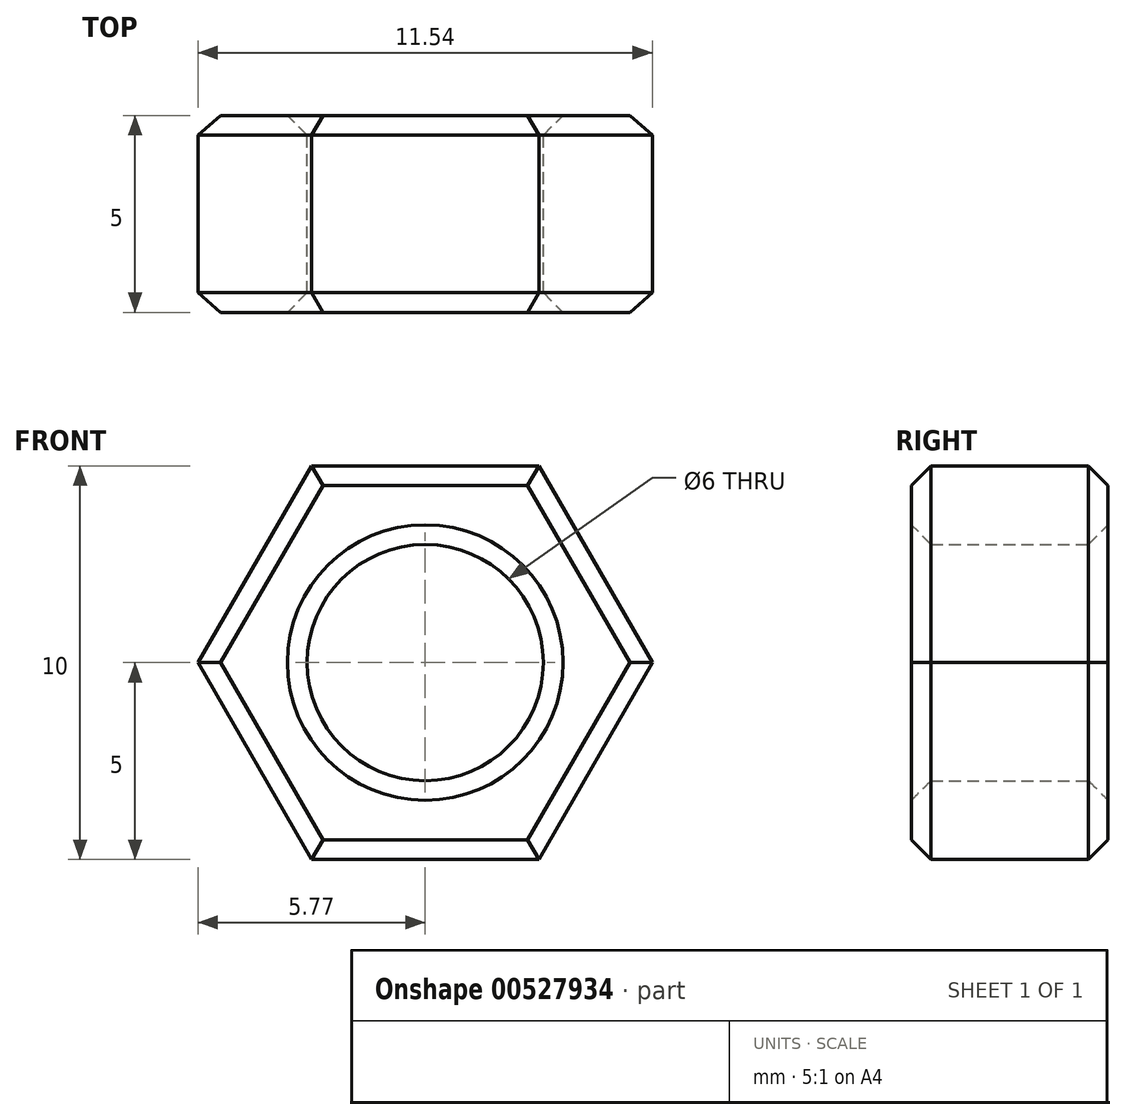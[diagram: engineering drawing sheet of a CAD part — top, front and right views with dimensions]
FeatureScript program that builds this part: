
annotation { "Feature Type Name" : "Feature", "Feature Type Description" : "" }
export const myFeature = defineFeature(function(context is Context, id is Id, definition is map)
    precondition{}
    {
        {
            var Q0;
            Q0=qCreatedBy(makeId("Front.planeOp"),FACE);
            var sketch = newSketch(context, id + "F0", { "sketchPlane" : qUnion([Q0])});
            skCircle(sketch, "E0.cCircle", {"center": v(0, 0) * mm, "radius": 5 * mm, "construction": true});
            skLineSegment(sketch, "E0.0", {"start": v(-2.89, 5) * mm, "end": v(2.89, 5) * mm});
            skLineSegment(sketch, "E0.1", {"start": v(2.89, 5) * mm, "end": v(5.77, 0) * mm});
            skLineSegment(sketch, "E0.2", {"start": v(5.77, 0) * mm, "end": v(2.89, -5) * mm});
            skLineSegment(sketch, "E0.3", {"start": v(2.89, -5) * mm, "end": v(-2.89, -5) * mm});
            skLineSegment(sketch, "E0.4", {"start": v(-2.89, -5) * mm, "end": v(-5.77, 0) * mm});
            skLineSegment(sketch, "E0.5", {"start": v(-5.77, 0) * mm, "end": v(-2.89, 5) * mm});
            skPoint(sketch, "E0.0.midPoint", {"position": v(0, 5) * mm});
            skCircle(sketch, "E1", {"center": v(0, 0) * mm, "radius": 3 * mm});
            skSolve(sketch);
        }
        {
            var Q0;
            Q0=makeQuery(id+"F0.imprint","IMPRINT",FACE,{"disambiguationData":[TD([[makeQuery(id+"F0.imprint","IMPRINT",EDGE,{"derivedFrom":sQuery(id+"F0.wireOp",EDGE,"E0.0")}),-1.0]])]});
            extrude(context, id + "F1", {"entities" : qUnion([Q0]), "depth" : 5 * mm, "offsetDistance" : 25 * mm});
        }
        {
            var Q0;
            Q0=makeQuery(id+"F1.opExtrude","CAP_FACE",FACE,{"disambiguationData":[OSD([sQuery(id+"F0.wireOp",EDGE,"E0.0"),sQuery(id+"F0.wireOp",EDGE,"E0.1"),sQuery(id+"F0.wireOp",EDGE,"E0.2"),sQuery(id+"F0.wireOp",EDGE,"E0.3"),sQuery(id+"F0.wireOp",EDGE,"E0.4"),sQuery(id+"F0.wireOp",EDGE,"E0.5"),sQuery(id+"F0.wireOp",EDGE,"E1")])],"isStart":false});
            var Q1;
            Q1=makeQuery(id+"F1.opExtrude","CAP_FACE",FACE,{"disambiguationData":[OSD([sQuery(id+"F0.wireOp",EDGE,"E0.0"),sQuery(id+"F0.wireOp",EDGE,"E0.1"),sQuery(id+"F0.wireOp",EDGE,"E0.2"),sQuery(id+"F0.wireOp",EDGE,"E0.3"),sQuery(id+"F0.wireOp",EDGE,"E0.4"),sQuery(id+"F0.wireOp",EDGE,"E0.5"),sQuery(id+"F0.wireOp",EDGE,"E1")])],"isStart":true});
            chamfer(context, id + "F2", {"entities" : qUnion([Q0, Q1]), "width" : 0.5 * mm, "tangentPropagation" : true});
        }
    });
